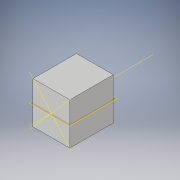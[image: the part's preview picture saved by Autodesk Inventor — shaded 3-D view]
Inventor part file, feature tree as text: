
AUTODESK INVENTOR PART (.ipt)
format: ipt  version: 2017 (Build 210142000, 142)  size: 98,816 bytes
history: native  units: in
note: dims shown in document units (in); Inventor stores cm internally (conversion verified against a paired STEP export)
features: other x8, sketch x2, extrude x1, plane x1
ambient origin geometry x8: Origin, YZ Plane, XZ Plane, XY Plane, X Axis, Y Axis, Z Axis, Center Point
bodies: Solid1 (feature_tree)
feature tree (12):
  extrude  "Extrusion1"  Depth=0.8661in
  other  "Work Point1"
  other  "Work Point2"
  other  "Work Point3"
  other  "Work Point4"
  plane  "Work Plane1"
  sketch  "Sketch5"  dims[d2=0.9843in d3=0.0in d9=90.0deg]
  sketch  "Sketch2"  dims[d0=1.0236in d1=0.8661in]
  other  "Work Axis1"
  other  "Work Axis2"
  other  "Work Point5"
  other  "Work Axis3"
